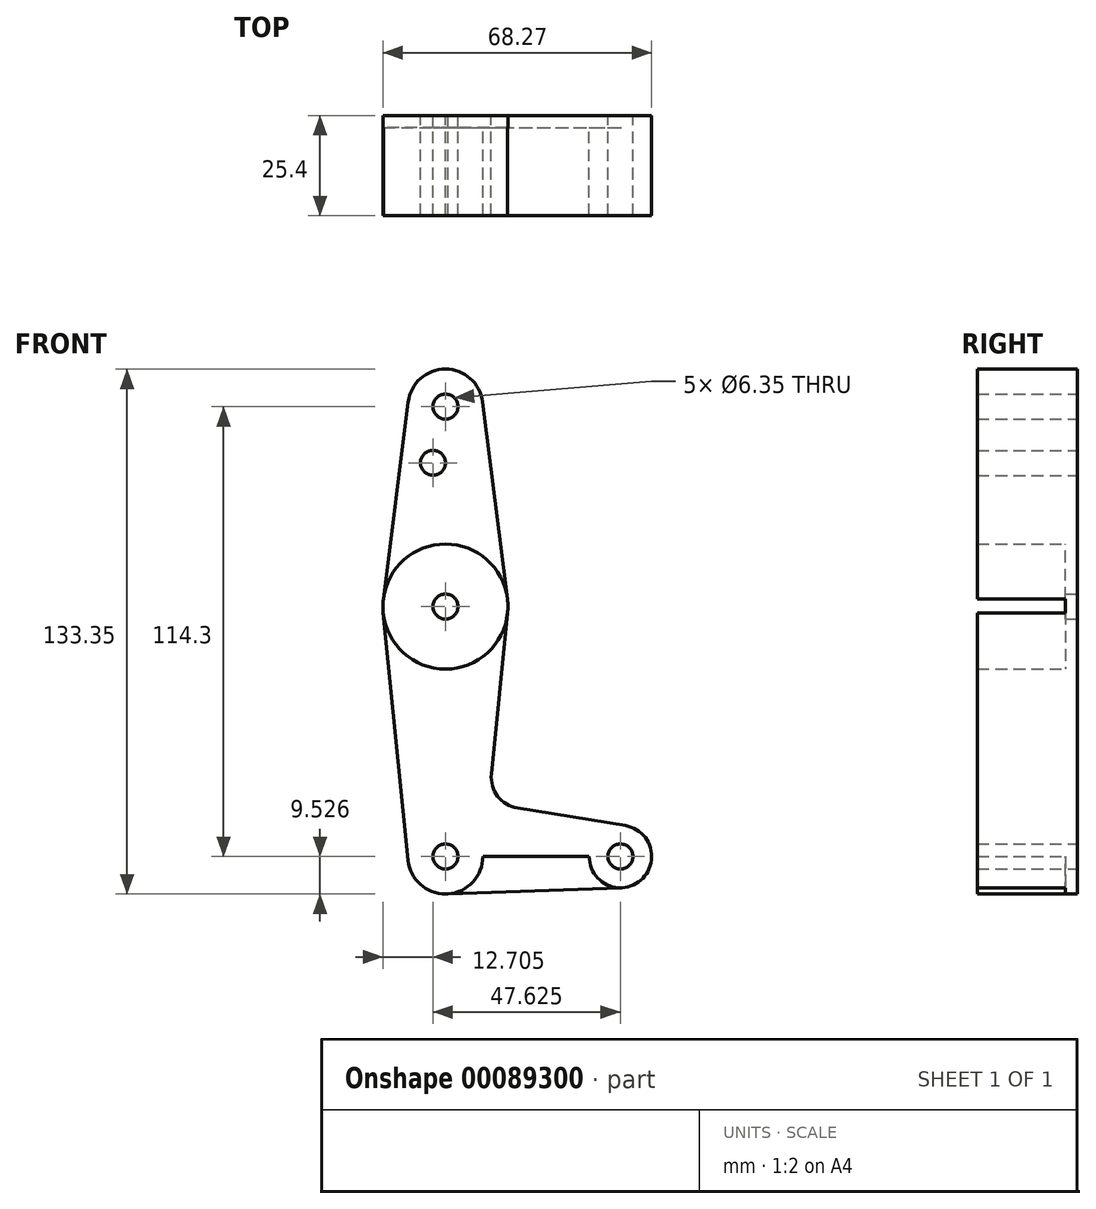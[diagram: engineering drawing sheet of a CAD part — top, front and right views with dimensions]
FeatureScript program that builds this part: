
annotation { "Feature Type Name" : "Feature", "Feature Type Description" : "" }
export const myFeature = defineFeature(function(context is Context, id is Id, definition is map)
    precondition{}
    {
        {
            var Q0;
            Q0=qCreatedBy(makeId("Front.planeOp"),FACE);
            var sketch = newSketch(context, id + "F0", { "sketchPlane" : qUnion([Q0])});
            skLineSegment(sketch, "E0", {"start": v(0, 75.78) * mm, "end": v(0, -38.52) * mm});
            skCircle(sketch, "E1", {"center": v(0, 75.78) * mm, "radius": 9.53 * mm});
            skCircle(sketch, "E2", {"center": v(0, -38.52) * mm, "radius": 9.53 * mm});
            skCircle(sketch, "E3", {"center": v(0, 24.98) * mm, "radius": 15.88 * mm});
            skLineSegment(sketch, "E4", {"start": v(0, -38.52) * mm, "end": v(44.45, -38.52) * mm});
            skCircle(sketch, "E5", {"center": v(44.45, -38.52) * mm, "radius": 7.94 * mm});
            skLineSegment(sketch, "E6", {"start": v(-9.45, 76.97) * mm, "end": v(-15.75, 26.96) * mm});
            skLineSegment(sketch, "E7", {"start": v(-15.8, 23.39) * mm, "end": v(-9.48, -39.48) * mm});
            skLineSegment(sketch, "E8", {"start": v(9.45, 76.97) * mm, "end": v(15.75, 26.96) * mm});
            skLineSegment(sketch, "E9", {"start": v(15.8, 23.39) * mm, "end": v(11.68, -17.6) * mm});
            skLineSegment(sketch, "E10", {"start": v(18.31, -26.24) * mm, "end": v(45.72, -30.69) * mm});
            skLineSegment(sketch, "E11", {"start": v(0, -48.05) * mm, "end": v(44.73, -46.46) * mm});
            skArc(sketch, "E12.filletArc", {"start": v(11.68, -17.6) * mm, "mid": v(13.28, -23.23) * mm, "end": v(18.31, -26.24) * mm});
            skCircle(sketch, "E13", {"center": v(0, 75.78) * mm, "radius": 3.18 * mm});
            skCircle(sketch, "E14", {"center": v(0, 24.98) * mm, "radius": 3.18 * mm});
            skCircle(sketch, "E15", {"center": v(0, -38.52) * mm, "radius": 3.18 * mm});
            skCircle(sketch, "E16", {"center": v(44.45, -38.52) * mm, "radius": 3.18 * mm});
            skCircle(sketch, "E17", {"center": v(-3.18, 61.5) * mm, "radius": 3.18 * mm});
            skSolve(sketch);
        }
        {
            var Q0;
            {var subQ5=sQuery(id+"F0.wireOp",EDGE,"E8");Q0=makeQuery(id+"F0.imprint","IMPRINT",FACE,{"disambiguationData":[TD([[makeQuery(id+"F0.imprint","IMPRINT",EDGE,{"derivedFrom":subQ5}),-1.0]])]});}
            var Q1;
            Q1=makeQuery(id+"F0.imprint","IMPRINT",FACE,{"disambiguationData":[TD([[makeQuery(id+"F0.imprint","IMPRINT",EDGE,{"derivedFrom":sQuery(id+"F0.wireOp",EDGE,"E13")}),-1.0]])]});
            var Q2;
            {var subQ0=sQuery(id+"F0.wireOp",EDGE,"E6");Q2=makeQuery(id+"F0.imprint","IMPRINT",FACE,{"disambiguationData":[TD([[makeQuery(id+"F0.imprint","IMPRINT",EDGE,{"derivedFrom":subQ0}),1.0]])]});}
            var Q3;
            {var subQ0=sQuery(id+"F0.wireOp",EDGE,"E3");var subQ3=sQuery(id+"F0.wireOp",EDGE,"E0");var subQ4=makeQuery(id+"F0.imprint","INTERSECT",VERTEX,{"disambiguationData":[OD(0.0)],"derivedFrom":[subQ3,subQ0]});Q3=makeQuery(id+"F0.imprint","IMPRINT",FACE,{"disambiguationData":[TD([[makeQuery(id+"F0.imprint","IMPRINT",EDGE,{"disambiguationData":[TD([[subQ4,-1.0]])],"derivedFrom":subQ3}),-1.0]])]});}
            var Q4;
            {var subQ0=sQuery(id+"F0.wireOp",EDGE,"E3");var subQ2=sQuery(id+"F0.wireOp",EDGE,"E0");var subQ5=makeQuery(id+"F0.imprint","INTERSECT",VERTEX,{"disambiguationData":[OD(0.0)],"derivedFrom":[subQ2,subQ0]});Q4=makeQuery(id+"F0.imprint","IMPRINT",FACE,{"disambiguationData":[TD([[makeQuery(id+"F0.imprint","IMPRINT",EDGE,{"disambiguationData":[TD([[subQ5,-1.0]])],"derivedFrom":subQ2}),1.0]])]});}
            var Q5;
            {var subQ5=sQuery(id+"F0.wireOp",EDGE,"E7");Q5=makeQuery(id+"F0.imprint","IMPRINT",FACE,{"disambiguationData":[TD([[makeQuery(id+"F0.imprint","IMPRINT",EDGE,{"derivedFrom":subQ5}),1.0]])]});}
            var Q6;
            {var subQ7=sQuery(id+"F0.wireOp",EDGE,"E9");Q6=makeQuery(id+"F0.imprint","IMPRINT",FACE,{"disambiguationData":[TD([[makeQuery(id+"F0.imprint","IMPRINT",EDGE,{"derivedFrom":subQ7}),-1.0]])]});}
            var Q7;
            {var subQ0=sQuery(id+"F0.wireOp",EDGE,"E11");var subQ1=sQuery(id+"F0.wireOp",EDGE,"E2");var subQ2=makeQuery(id+"F0.imprint","INTERSECT",VERTEX,{"disambiguationData":[OD(1.0)],"derivedFrom":[subQ1,subQ0]});Q7=makeQuery(id+"F0.imprint","IMPRINT",FACE,{"disambiguationData":[TD([[makeQuery(id+"F0.imprint","IMPRINT",EDGE,{"disambiguationData":[TD([[subQ2,-1.0]])],"derivedFrom":subQ1}),-1.0]])]});}
            var Q8;
            {var subQ1=sQuery(id+"F0.wireOp",EDGE,"E2");var subQ6=sQuery(id+"F0.wireOp",EDGE,"E0");var subQ11=makeQuery(id+"F0.imprint","INTERSECT",VERTEX,{"derivedFrom":[subQ6,subQ1]});Q8=makeQuery(id+"F0.imprint","IMPRINT",FACE,{"disambiguationData":[TD([[makeQuery(id+"F0.imprint","IMPRINT",EDGE,{"disambiguationData":[TD([[subQ11,-1.0]])],"derivedFrom":subQ6}),-1.0]])]});}
            var Q9;
            {var subQ0=sQuery(id+"F0.wireOp",EDGE,"E2");var subQ1=sQuery(id+"F0.wireOp",EDGE,"E0");var subQ2=makeQuery(id+"F0.imprint","INTERSECT",VERTEX,{"derivedFrom":[subQ1,subQ0]});Q9=makeQuery(id+"F0.imprint","IMPRINT",FACE,{"disambiguationData":[TD([[makeQuery(id+"F0.imprint","IMPRINT",EDGE,{"disambiguationData":[TD([[subQ2,-1.0]])],"derivedFrom":subQ1}),1.0]])]});}
            var Q10;
            Q10=makeQuery(id+"F0.imprint","IMPRINT",FACE,{"disambiguationData":[TD([[makeQuery(id+"F0.imprint","IMPRINT",EDGE,{"derivedFrom":sQuery(id+"F0.wireOp",EDGE,"E16")}),-1.0]])]});
            extrude(context, id + "F1", {"entities" : qUnion([Q0, Q1, Q2, Q3, Q4, Q5, Q6, Q7, Q8, Q9, Q10]), "depth" : 25.4 * mm});
        }
        {
            var Q0;
            Q0 = qSketchRegion(id + "F0", true);
            extrude(context, id + "F2", {"entities" : qUnion([Q0]), "operationType" : NewBodyOperationType.ADD, "depth" : 3.05 * mm});
        }
    });
